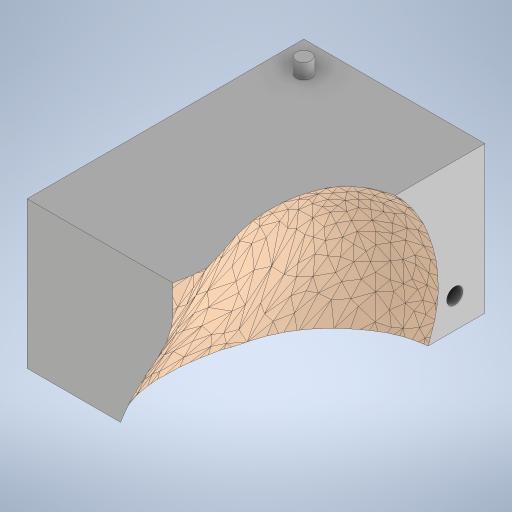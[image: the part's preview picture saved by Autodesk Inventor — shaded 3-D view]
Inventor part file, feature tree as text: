
AUTODESK INVENTOR PART (.ipt)
format: ipt  version: 2024 (Build 280153000, 153)  size: 10,802,176 bytes
history: native  units: mm
features: other x6, extrude x6, sketch x6, plane x2
ambient origin geometry x8: Origin, YZ Plane, XZ Plane, XY Plane, X Axis, Y Axis, Z Axis, Center Point
bodies: Body1 (feature_tree)
feature tree (20):
  other  "M.ipt"
  plane  "Plano de trabajo1"
  extrude  "Extrusión1"  [1 undecoded]
  other  "Combinar1"
  sketch  "Boceto3"  dims[d2=550.0mm d3=520.0mm]
  sketch  "Boceto4"  dims[d4=550.0mm d5=0.0mm d6=129.8482mm]
  plane  "Plano de trabajo2"
  sketch  "Boceto5"  dims[d17=180.0mm d18=180.0mm]
  extrude  "Extrusión2"  Depth=520.0mm
  extrude  "Extrusión3"  Depth=129.8482mm
  extrude  "Extrusión4"  Depth=180.0mm
  extrude  "Extrusión5"  Depth=180.0mm
  extrude  "Extrusión6"  Depth=180.0mm
  other  "Sólido1::M.ipt"
  other  "OperaciónIdentificador1"
  sketch  "Boceto1"  dims[d0=25.0mm d1=-365.0mm]
  other  "Sólido2"
  sketch  "Boceto6"  dims[d22=326.0mm d23=180.0mm]
  sketch  "Boceto7"  dims[d24=180.0mm d25=180.0mm d26=10.0mm d27=0.0mm d28=1000.0mm d29=0.0mm d30=1000.0mm d31=0.0mm d32=30.0mm d33=30.0mm d34=16.0mm d35=16.0mm d36=0.0mm d37=30.0mm d38=30.0mm d39=15.0mm d40=15.0mm d41=161.0mm d42=0.0mm d43=0.0mm d14=0.5mm d15=0.872665mm d16=0.5mm d19=0.5mm d20=0.872665mm d21=0.5mm]
  other  "Sólido1"
note: 1 required parameter value undecoded (feature->parameter linkage not recoverable at this tier; creation-order binding heuristic only, values carry confidence <= 0.55)
